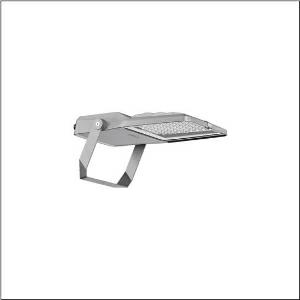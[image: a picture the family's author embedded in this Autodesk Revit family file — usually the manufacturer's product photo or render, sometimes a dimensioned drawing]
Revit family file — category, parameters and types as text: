
# Revit family: floodlight_fl_21_mini___pl61_5xa7773c4c1a_fa47
name_source: partatom
category: Lighting Fixtures
units: mm (PartAtom-declared; Revit-internal decimal feet)

## family parameters
Cut with Voids When Loaded = No
Host = Face
Light Source = No
Part Type = Normal
Room Calculation Point = No
Round Connector Dimension = Use Diameter
Shared = No

## types (1)
- --- (1 x LED, 19990 lm, 163.5 W, 4000K)
    Apparent Load = 163 VA
    CIE Flux Codes = 33 65 98 100 100
    Color Rendering = 70
    Color Temperature = 4000K
    Default Elevation = 1800 mm
    Description = Floodlight FL 21 mini, floodlight, primary light control with lens, of PMMA, primary optical cover: protective disc, of toughened safety glass, transparent, light distribution: PL61, light emission: direct distribution, installation type: surface-mounted, LED, High Power LED, rated luminous flux: 19.990lm, luminous efficacy: 122lm/W, light colour: 740, colour temperature: 4000K, control gear: ON/OFF Multilumen, control: pre-setting: linear dimming characteristic, Temp-Guard, with terminal, 6-pole, mains connection: 220..240V, AC, 50/60Hz, start of lifetime: 164W, luminaire housing, of diecast aluminium, powder-coated, SITECO metallic grey (DB 702S), corrosivity category C5 mid according to DIN EN ISO 12944, suitable for swimming pools, chlorine-resistant, sealing non-destructively replaceable, mounting bracket, of steel, galvanised, powder-coated, SITECO metallic grey (DB 702S), ON/OFF, protection rating (complete): IP66, insulation class (complete): insulation class I (protective earthing), certification: CE, ENEC, VDE, protection symbol: D, impact resistance: IK08, permissible operating ambient temperature: -40..+40°C, permissible operating ambient temperature for outdoor applications: -40..+50°C, standard: DIN EN 12944, LABS conformity tested according to VDMA 24364:2018-05, packaging unit: 1 piece

Light Distribution: PL61
    Height = 70 mm
    Lamp = 1 x LED
    Lamp Light Flux = 19990 lm
    Lamp Power = 163.5 W
    Lamp count = 1
    Length = 485 mm
    Luminous efficacy = 122 lm/W
    Manufacturer = Siteco
    ModVariant = No
    Model = 5XA7773C4C1A
    Number of Poles = 1
    OnlyDefault = Yes
    Power Factor = 1
    Product Name = Floodlight FL 21 mini | PL61
    Product group = floodlight | pylon annexe
    ProductGroupID = 6201
    Protection Class = Protection class I
    Protection Degree = IP 66
    RLX_Detail_Level = 1
    RLX_Emergency_Light_Flux = 0 lm
    RLX_Emergency_Type = 0
    RLX_Emergency_Type_DB = No
    RlxData = <blob elided: 94301 chars, md5=2618dfb0>
    Socket = socket
    Standby Power = 0 W
    System Light Flux = 19990 lm
    System Power = 163 W
    Type Comments = factory setting: luminous flux: 100 % | (ON | - | - | - | - | - | - | -) | 825 mA
    Type Image = l_1006845.jpg
    URL = http://relux.com
    VarID = @adj_172317
    Voltage = 0 V
    Weight = 0.00 kg
    Width = 337 mm

## geometry (parser evidence)
native form markers: Blend x4, Sweep x15
no freeform markers — native parametric forms only
